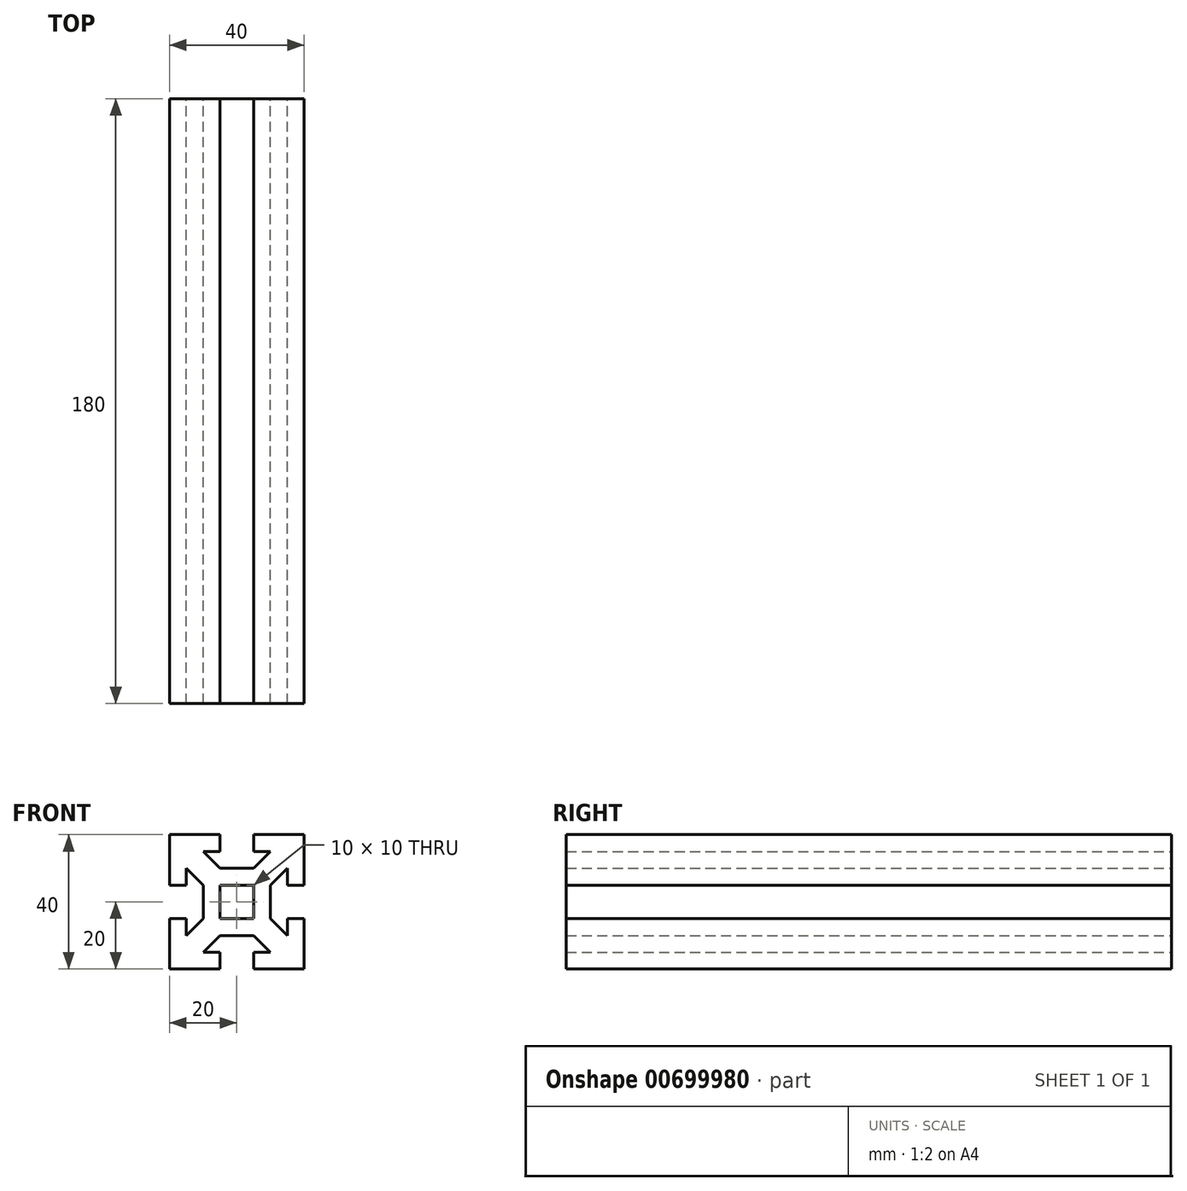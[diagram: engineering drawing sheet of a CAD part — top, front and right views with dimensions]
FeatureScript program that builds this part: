
annotation { "Feature Type Name" : "Feature", "Feature Type Description" : "" }
export const myFeature = defineFeature(function(context is Context, id is Id, definition is map)
    precondition{}
    {
        {
            var Q0;
            Q0=qCreatedBy(makeId("Front.planeOp"),FACE);
            var sketch = newSketch(context, id + "F0", { "sketchPlane" : qUnion([Q0])});
            skLineSegment(sketch, "E0.bottom", {"start": v(20, 20) * mm, "end": v(5, 20) * mm});
            skLineSegment(sketch, "E0.top", {"start": v(20, -20) * mm, "end": v(5, -20) * mm});
            skLineSegment(sketch, "E0.left", {"start": v(20, 20) * mm, "end": v(20, 5) * mm});
            skLineSegment(sketch, "E0.right", {"start": v(-20, 20) * mm, "end": v(-20, 5) * mm});
            skPoint(sketch, "E0.middle", {"position": v(0, 0) * mm});
            skLineSegment(sketch, "E1", {"start": v(0, 20) * mm, "end": v(0, -20) * mm, "construction": true});
            skLineSegment(sketch, "E2", {"start": v(-20, 0) * mm, "end": v(20, 0) * mm, "construction": true});
            skLineSegment(sketch, "E3", {"start": v(-20, 5) * mm, "end": v(-15, 5) * mm});
            skLineSegment(sketch, "E4", {"start": v(-20, -5) * mm, "end": v(-15, -5) * mm});
            skLineSegment(sketch, "E5", {"start": v(-5, 20) * mm, "end": v(-5, 15) * mm});
            skLineSegment(sketch, "E6", {"start": v(5, 20) * mm, "end": v(5, 15) * mm});
            skLineSegment(sketch, "E7", {"start": v(-10, 15) * mm, "end": v(-5, 15) * mm});
            skLineSegment(sketch, "E8", {"start": v(-10, -15) * mm, "end": v(-5, -15) * mm});
            skLineSegment(sketch, "E9", {"start": v(15, 10) * mm, "end": v(15, 5) * mm});
            skLineSegment(sketch, "E10", {"start": v(-15, 10) * mm, "end": v(-10, 5) * mm});
            skLineSegment(sketch, "E11", {"start": v(-10, 15) * mm, "end": v(-5, 10) * mm});
            skLineSegment(sketch, "E12", {"start": v(-15, -10) * mm, "end": v(-10, -5) * mm});
            skLineSegment(sketch, "E13", {"start": v(-10, -15) * mm, "end": v(-5, -10) * mm});
            skLineSegment(sketch, "E14.trimOffspring", {"start": v(20, -5) * mm, "end": v(20, -20) * mm});
            skLineSegment(sketch, "E15.trimOffspring", {"start": v(-20, -5) * mm, "end": v(-20, -20) * mm});
            skLineSegment(sketch, "E16.trimOffspring", {"start": v(-5, -20) * mm, "end": v(-20, -20) * mm});
            skLineSegment(sketch, "E17.trimOffspring", {"start": v(-5, 20) * mm, "end": v(-20, 20) * mm});
            skLineSegment(sketch, "E18.trimOffspring", {"start": v(5, 15) * mm, "end": v(10, 15) * mm});
            skLineSegment(sketch, "E19.trimOffspring", {"start": v(-15, -5) * mm, "end": v(-15, -10) * mm});
            skLineSegment(sketch, "E20.trimOffspring", {"start": v(15, -5) * mm, "end": v(15, -10) * mm});
            skLineSegment(sketch, "E21.trimOffspring", {"start": v(5, -15) * mm, "end": v(10, -15) * mm});
            skLineSegment(sketch, "E22.trimOffspring", {"start": v(-5, 5) * mm, "end": v(-5, -5) * mm});
            skLineSegment(sketch, "E23.trimOffspring", {"start": v(5, 5) * mm, "end": v(5, -5) * mm});
            skLineSegment(sketch, "E24.trimOffspring", {"start": v(15, 5) * mm, "end": v(20, 5) * mm});
            skLineSegment(sketch, "E25.trimOffspring", {"start": v(15, -5) * mm, "end": v(20, -5) * mm});
            skLineSegment(sketch, "E26.trimOffspring", {"start": v(5, -15) * mm, "end": v(5, -20) * mm});
            skLineSegment(sketch, "E27.trimOffspring", {"start": v(-5, -15) * mm, "end": v(-5, -20) * mm});
            skLineSegment(sketch, "E28.trimOffspring", {"start": v(-5, -5) * mm, "end": v(5, -5) * mm});
            skLineSegment(sketch, "E29.trimOffspring", {"start": v(-5, 5) * mm, "end": v(5, 5) * mm});
            skLineSegment(sketch, "E30", {"start": v(10, 5) * mm, "end": v(10, -5) * mm});
            skLineSegment(sketch, "E31", {"start": v(-5, 10) * mm, "end": v(5, 10) * mm});
            skLineSegment(sketch, "E32", {"start": v(-10, 5) * mm, "end": v(-10, -5) * mm});
            skLineSegment(sketch, "E33", {"start": v(-5, -10) * mm, "end": v(5, -10) * mm});
            skLineSegment(sketch, "E34.trimOffspring", {"start": v(-15, 10) * mm, "end": v(-15, 5) * mm});
            skPoint(sketch, "E35.orphan", {"position": v(20, 15) * mm});
            skPoint(sketch, "E36.orphan", {"position": v(20, -15) * mm});
            skPoint(sketch, "E37.orphan", {"position": v(15, -20) * mm});
            skPoint(sketch, "E38.orphan", {"position": v(-15, -20) * mm});
            skLineSegment(sketch, "E39.trimOffspring", {"start": v(-5, 0) * mm, "end": v(0, -5) * mm});
            skLineSegment(sketch, "E40.trimOffspring", {"start": v(-5, 0) * mm, "end": v(0, 5) * mm});
            skLineSegment(sketch, "E41.trimOffspring", {"start": v(0, 5) * mm, "end": v(5, 0) * mm});
            skLineSegment(sketch, "E42.trimOffspring", {"start": v(5, 10) * mm, "end": v(10, 15) * mm});
            skLineSegment(sketch, "E43.trimOffspring", {"start": v(10, 5) * mm, "end": v(15, 10) * mm});
            skLineSegment(sketch, "E44.trimOffspring", {"start": v(10, -5) * mm, "end": v(15, -10) * mm});
            skLineSegment(sketch, "E45.trimOffspring", {"start": v(5, -10) * mm, "end": v(10, -15) * mm});
            skLineSegment(sketch, "E46.trimOffspring", {"start": v(0, -5) * mm, "end": v(5, 0) * mm});
            skSolve(sketch);
        }
        {
            var Q0;
            Q0=makeQuery(id+"F0.imprint","IMPRINT",FACE,{"disambiguationData":[TD([[makeQuery(id+"F0.imprint","IMPRINT",EDGE,{"derivedFrom":sQuery(id+"F0.wireOp",EDGE,"E0.bottom")}),1.0]])]});
            extrude(context, id + "F1", {"entities" : qUnion([Q0]), "depth" : 180 * mm, "offsetDistance" : 25 * mm});
        }
    });
